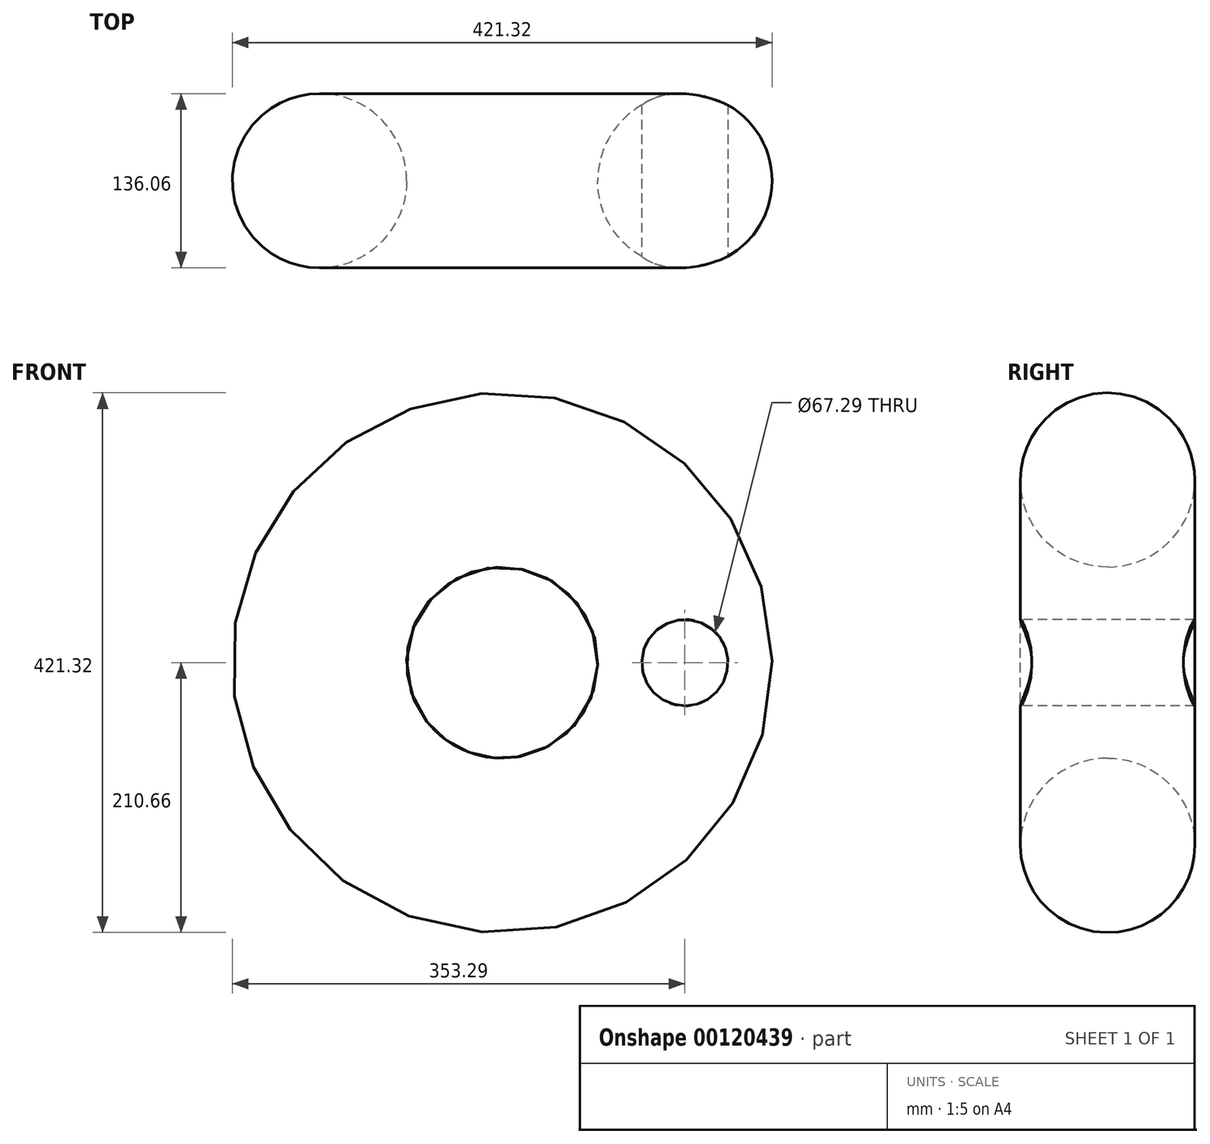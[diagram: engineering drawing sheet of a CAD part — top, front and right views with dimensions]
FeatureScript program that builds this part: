
annotation { "Feature Type Name" : "Feature", "Feature Type Description" : "" }
export const myFeature = defineFeature(function(context is Context, id is Id, definition is map)
    precondition{}
    {
        {
            var Q0;
            Q0=qCreatedBy(makeId("Top.planeOp"),FACE);
            var sketch = newSketch(context, id + "F0", { "sketchPlane" : qUnion([Q0])});
            skCircle(sketch, "E0", {"center": v(0, 0) * mm, "radius": 68.03 * mm});
            skLineSegment(sketch, "E1", {"start": v(-142.63, 81.43) * mm, "end": v(-142.63, -98.01) * mm});
            skLineSegment(sketch, "E2", {"start": v(0, 0) * mm, "end": v(0, 68.03) * mm});
            skSolve(sketch);
        }
        {
            var Q0;
            Q0=makeQuery(id+"F0.imprint","IMPRINT",FACE,{"disambiguationData":[TD([[makeQuery(id+"F0.imprint","IMPRINT",EDGE,{"derivedFrom":sQuery(id+"F0.wireOp",EDGE,"E0")}),1.0]])]});
            var Q1;
            Q1=sQuery(id+"F0.wireOp",EDGE,"E1");
            revolve(context, id + "F1", {"entities" : qUnion([Q0]), "axis" : qUnion([Q1]), "revolveType" : RevolveType.FULL});
        }
        {
            var Q0;
            Q0=qCreatedBy(makeId("Front.planeOp"),FACE);
            var sketch = newSketch(context, id + "F2", { "sketchPlane" : qUnion([Q0])});
            skCircle(sketch, "E3", {"center": v(0, 0) * mm, "radius": 33.65 * mm});
            skSolve(sketch);
        }
        {
            var Q0;
            Q0 = qSketchRegion(id + "F2", true);
            extrude(context, id + "F3", {"entities" : qUnion([Q0]), "operationType" : NewBodyOperationType.REMOVE, "endBound" : BoundingType.THROUGH_ALL, "oppositeDirection" : true, "depth" : 25.4 * mm, "hasSecondDirection" : true, "secondDirectionBound" : SecondDirectionBoundingType.THROUGH_ALL, "secondDirectionOppositeDirection" : false, "secondDirectionDepth" : 25.4 * mm});
        }
    });
